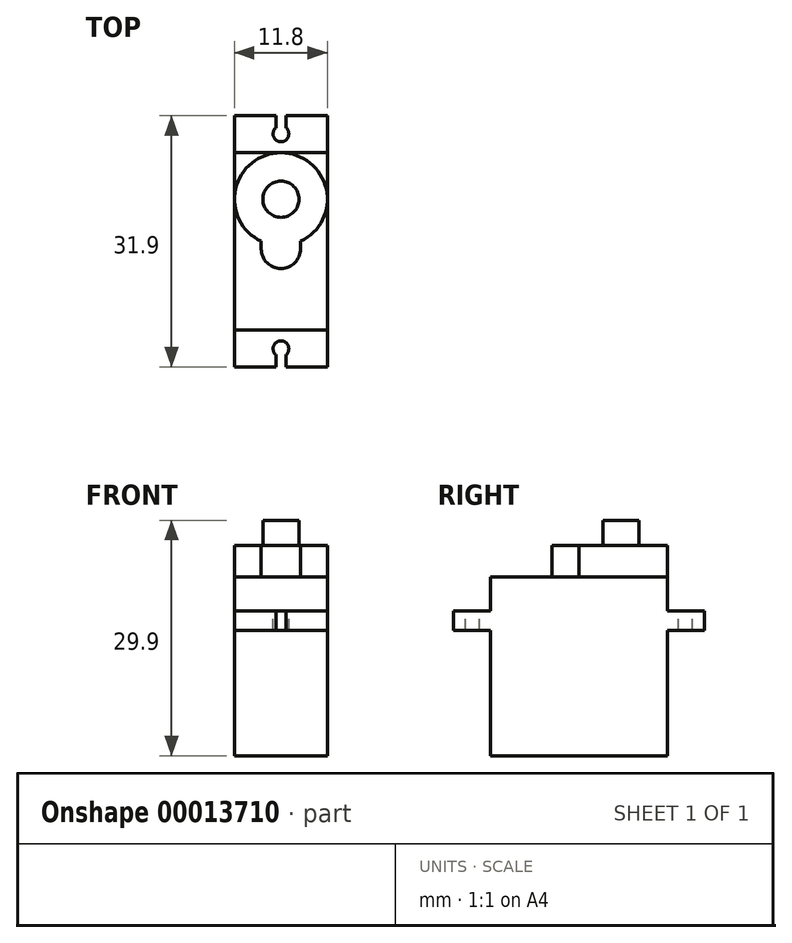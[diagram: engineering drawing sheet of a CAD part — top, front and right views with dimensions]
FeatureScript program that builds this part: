
annotation { "Feature Type Name" : "Feature", "Feature Type Description" : "" }
export const myFeature = defineFeature(function(context is Context, id is Id, definition is map)
    precondition{}
    {
        {
            var Q0;
            Q0=qCreatedBy(makeId("Top.planeOp"),FACE);
            var sketch = newSketch(context, id + "F0", { "sketchPlane" : qUnion([Q0])});
            skLineSegment(sketch, "E0.rect.bottom", {"start": v(5.9, -11.25) * mm, "end": v(-5.9, -11.25) * mm});
            skLineSegment(sketch, "E0.rect.top", {"start": v(5.9, 11.25) * mm, "end": v(-5.9, 11.25) * mm});
            skLineSegment(sketch, "E0.rect.left", {"start": v(5.9, -15.95) * mm, "end": v(5.9, 15.95) * mm});
            skLineSegment(sketch, "E0.rect.right", {"start": v(-5.9, -15.95) * mm, "end": v(-5.9, 15.95) * mm});
            skPoint(sketch, "E0.rect.middle", {"position": v(0, 0) * mm});
            skLineSegment(sketch, "E1", {"start": v(0, 11.25) * mm, "end": v(0, -11.25) * mm, "construction": true});
            skArc(sketch, "E2", {"start": v(2.5, 0) * mm, "mid": v(0, 11.25) * mm, "end": v(-2.5, 0) * mm});
            skArc(sketch, "E3", {"start": v(-2.5, -0.95) * mm, "mid": v(0, -3.45) * mm, "end": v(2.5, -0.95) * mm});
            skLineSegment(sketch, "E4", {"start": v(2.5, -0.95) * mm, "end": v(2.5, 0) * mm});
            skLineSegment(sketch, "E5", {"start": v(-2.5, -0.95) * mm, "end": v(-2.5, 0) * mm});
            skCircle(sketch, "E6", {"center": v(0, 5.35) * mm, "radius": 2.3 * mm});
            skLineSegment(sketch, "E7", {"start": v(-5.9, 15.95) * mm, "end": v(5.9, 15.95) * mm});
            skLineSegment(sketch, "E8", {"start": v(-5.9, -15.95) * mm, "end": v(5.9, -15.95) * mm});
            skArc(sketch, "E9", {"start": v(-0.65, 14.4) * mm, "mid": v(0, 12.65) * mm, "end": v(0.65, 14.4) * mm});
            skLineSegment(sketch, "E10", {"start": v(0, 15.95) * mm, "end": v(0, 13.65) * mm, "construction": true});
            skLineSegment(sketch, "E11", {"start": v(0.65, 15.95) * mm, "end": v(0.65, 14.4) * mm});
            skLineSegment(sketch, "E12", {"start": v(-0.65, 15.95) * mm, "end": v(-0.65, 14.4) * mm});
            skLineSegment(sketch, "E13", {"start": v(0, 14.8) * mm, "end": v(-0.65, 14.8) * mm, "construction": true});
            skLineSegment(sketch, "E14", {"start": v(0, 14.8) * mm, "end": v(0.65, 14.8) * mm, "construction": true});
            skArc(sketch, "E15", {"start": v(0.65, -14.4) * mm, "mid": v(0, -12.65) * mm, "end": v(-0.65, -14.4) * mm});
            skLineSegment(sketch, "E16", {"start": v(0, -13.65) * mm, "end": v(0, -15.95) * mm, "construction": true});
            skLineSegment(sketch, "E17", {"start": v(0.65, -15.95) * mm, "end": v(0.65, -14.4) * mm});
            skLineSegment(sketch, "E18", {"start": v(-0.65, -15.95) * mm, "end": v(-0.65, -14.4) * mm});
            skLineSegment(sketch, "E19", {"start": v(0, -14.8) * mm, "end": v(0.65, -14.8) * mm, "construction": true});
            skLineSegment(sketch, "E20", {"start": v(0, -14.8) * mm, "end": v(-0.65, -14.8) * mm, "construction": true});
            skLineSegment(sketch, "E21", {"start": v(2.5, 0) * mm, "end": v(2.5, 0) * mm});
            skLineSegment(sketch, "E22", {"start": v(-2.5, 0) * mm, "end": v(-2.5, 0) * mm});
            skSolve(sketch);
        }
        {
            var Q0;
            Q0=makeQuery(id+"F0.imprint","IMPRINT",FACE,{"disambiguationData":[TD([[makeQuery(id+"F0.imprint","IMPRINT",EDGE,{"derivedFrom":sQuery(id+"F0.wireOp",EDGE,"E3")}),1.0]])]});
            extrude(context, id + "F1", {"entities" : qUnion([Q0]), "depth" : 4 * mm});
        }
        {
            var Q0;
            Q0=makeQuery(id+"F0.imprint","IMPRINT",FACE,{"disambiguationData":[TD([[makeQuery(id+"F0.imprint","IMPRINT",EDGE,{"derivedFrom":sQuery(id+"F0.wireOp",EDGE,"E6")}),1.0]])]});
            extrude(context, id + "F2", {"entities" : qUnion([Q0]), "operationType" : NewBodyOperationType.ADD, "depth" : (3.2 + 4) * mm});
        }
        {
            var Q0;
            {var subQ7=sQuery(id+"F0.wireOp",EDGE,"E0.rect.bottom");Q0=makeQuery(id+"F0.imprint","IMPRINT",FACE,{"disambiguationData":[TD([[makeQuery(id+"F0.imprint","IMPRINT",EDGE,{"derivedFrom":subQ7}),-1.0]])]});}
            var Q1;
            Q1=makeQuery(id+"F0.imprint","IMPRINT",FACE,{"disambiguationData":[TD([[makeQuery(id+"F0.imprint","IMPRINT",EDGE,{"derivedFrom":sQuery(id+"F0.wireOp",EDGE,"E3")}),1.0]])]});
            var Q2;
            Q2=makeQuery(id+"F0.imprint","IMPRINT",FACE,{"disambiguationData":[TD([[makeQuery(id+"F0.imprint","IMPRINT",EDGE,{"derivedFrom":sQuery(id+"F0.wireOp",EDGE,"E6")}),1.0]])]});
            var Q3;
            {var subQ1=sQuery(id+"F0.wireOp",EDGE,"E0.rect.top");var subQ3=sQuery(id+"F0.wireOp",EDGE,"E0.rect.right");var subQ5=makeQuery(id+"F0.imprint","INTERSECT",VERTEX,{"derivedFrom":[subQ1,subQ3]});Q3=makeQuery(id+"F0.imprint","IMPRINT",FACE,{"disambiguationData":[TD([[makeQuery(id+"F0.imprint","IMPRINT",EDGE,{"disambiguationData":[TD([[subQ5,1.0]])],"derivedFrom":subQ1}),1.0]])]});}
            var Q4;
            {var subQ1=sQuery(id+"F0.wireOp",EDGE,"E0.rect.top");var subQ3=sQuery(id+"F0.wireOp",EDGE,"E0.rect.left");var subQ5=makeQuery(id+"F0.imprint","INTERSECT",VERTEX,{"derivedFrom":[subQ1,subQ3]});Q4=makeQuery(id+"F0.imprint","IMPRINT",FACE,{"disambiguationData":[TD([[makeQuery(id+"F0.imprint","IMPRINT",EDGE,{"disambiguationData":[TD([[subQ5,-1.0]])],"derivedFrom":subQ1}),1.0]])]});}
            extrude(context, id + "F3", {"entities" : qUnion([Q0, Q1, Q2, Q3, Q4]), "operationType" : NewBodyOperationType.ADD, "oppositeDirection" : true, "depth" : 22.7 * mm});
        }
        {
            var Q0;
            Q0=makeQuery(id+"F0.imprint","IMPRINT",FACE,{"disambiguationData":[TD([[makeQuery(id+"F0.imprint","IMPRINT",EDGE,{"derivedFrom":sQuery(id+"F0.wireOp",EDGE,"E9")}),-1.0]])]});
            var Q1;
            {var subQ7=sQuery(id+"F0.wireOp",EDGE,"E0.rect.bottom");Q1=makeQuery(id+"F0.imprint","IMPRINT",FACE,{"disambiguationData":[TD([[makeQuery(id+"F0.imprint","IMPRINT",EDGE,{"derivedFrom":subQ7}),1.0]])]});}
            extrude(context, id + "F4", {"entities" : qUnion([Q0, Q1]), "operationType" : NewBodyOperationType.ADD, "oppositeDirection" : true, "depth" : (22.7 - 18.4 + 2.5) * mm});
        }
        {
            var Q0;
            Q0=makeQuery(id+"F0.imprint","IMPRINT",FACE,{"disambiguationData":[TD([[makeQuery(id+"F0.imprint","IMPRINT",EDGE,{"derivedFrom":sQuery(id+"F0.wireOp",EDGE,"E9")}),-1.0]])]});
            var Q1;
            {var subQ7=sQuery(id+"F0.wireOp",EDGE,"E0.rect.bottom");Q1=makeQuery(id+"F0.imprint","IMPRINT",FACE,{"disambiguationData":[TD([[makeQuery(id+"F0.imprint","IMPRINT",EDGE,{"derivedFrom":subQ7}),1.0]])]});}
            extrude(context, id + "F5", {"entities" : qUnion([Q0, Q1]), "operationType" : NewBodyOperationType.REMOVE, "oppositeDirection" : true, "depth" : (22.7 - 18.4) * mm});
        }
    });
